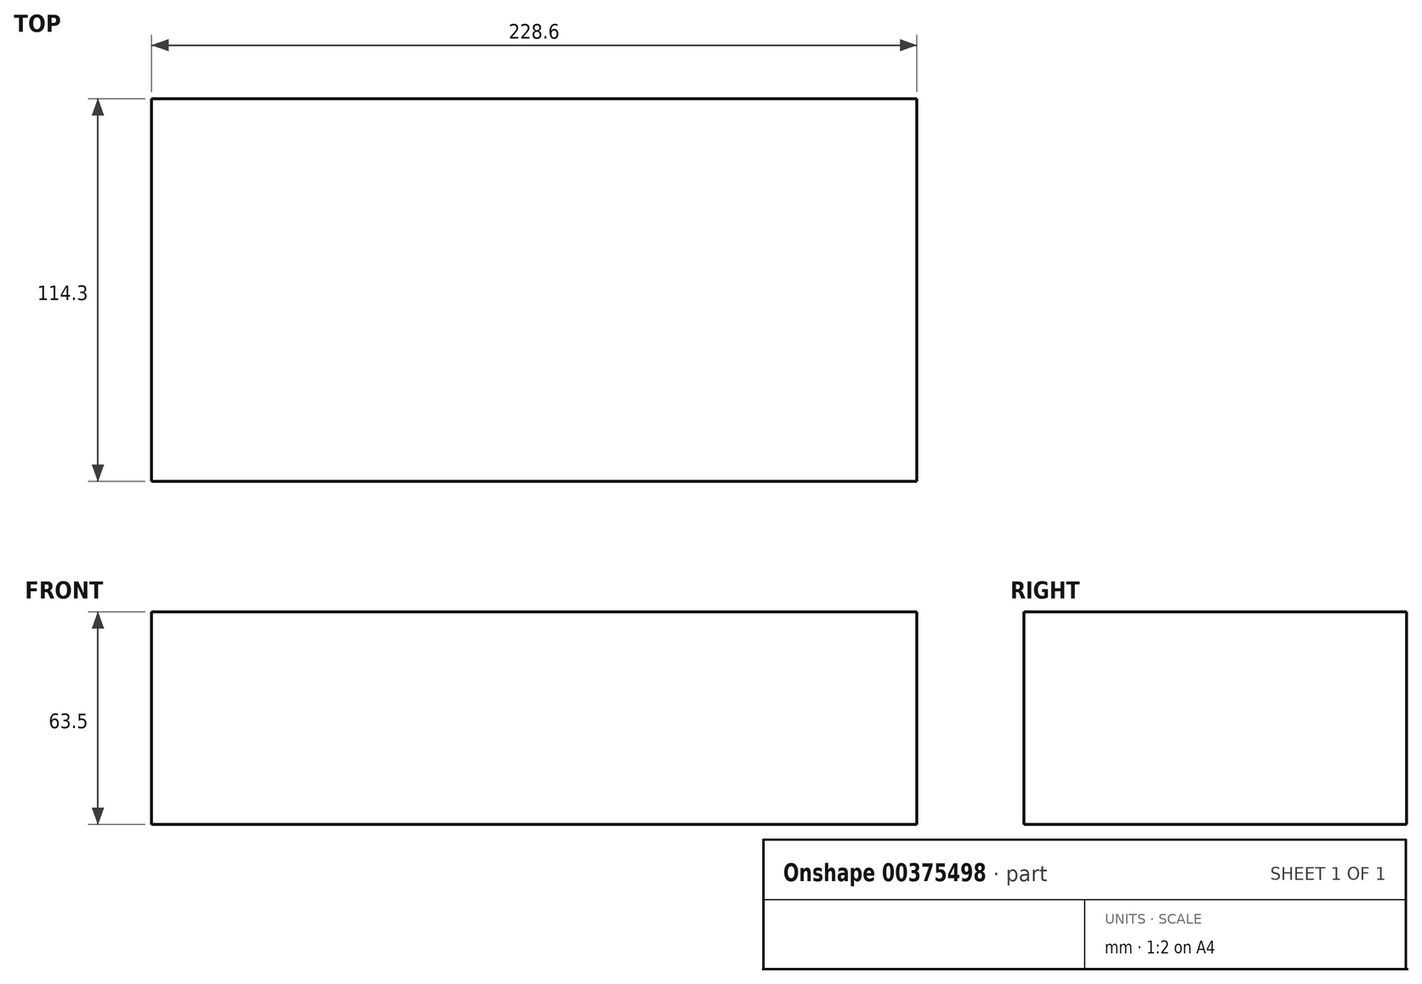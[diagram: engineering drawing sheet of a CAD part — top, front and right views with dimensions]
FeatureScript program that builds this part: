
annotation { "Feature Type Name" : "Feature", "Feature Type Description" : "" }
export const myFeature = defineFeature(function(context is Context, id is Id, definition is map)
    precondition{}
    {
        {
            var Q0;
            Q0=qCreatedBy(makeId("Top.planeOp"),FACE);
            var sketch = newSketch(context, id + "F0", { "sketchPlane" : qUnion([Q0])});
            skLineSegment(sketch, "E0.bottom", {"start": v(114.3, 57.15) * mm, "end": v(-114.3, 57.15) * mm});
            skLineSegment(sketch, "E0.top", {"start": v(114.3, -57.15) * mm, "end": v(-114.3, -57.15) * mm});
            skLineSegment(sketch, "E0.left", {"start": v(114.3, 57.15) * mm, "end": v(114.3, -57.15) * mm});
            skLineSegment(sketch, "E0.right", {"start": v(-114.3, 57.15) * mm, "end": v(-114.3, -57.15) * mm});
            skPoint(sketch, "E0.middle", {"position": v(0, 0) * mm});
            skSolve(sketch);
        }
        {
            var Q0;
            Q0 = qSketchRegion(id + "F0", true);
            extrude(context, id + "F1", {"entities" : qUnion([Q0]), "depth" : 63.5 * mm});
        }
    });
